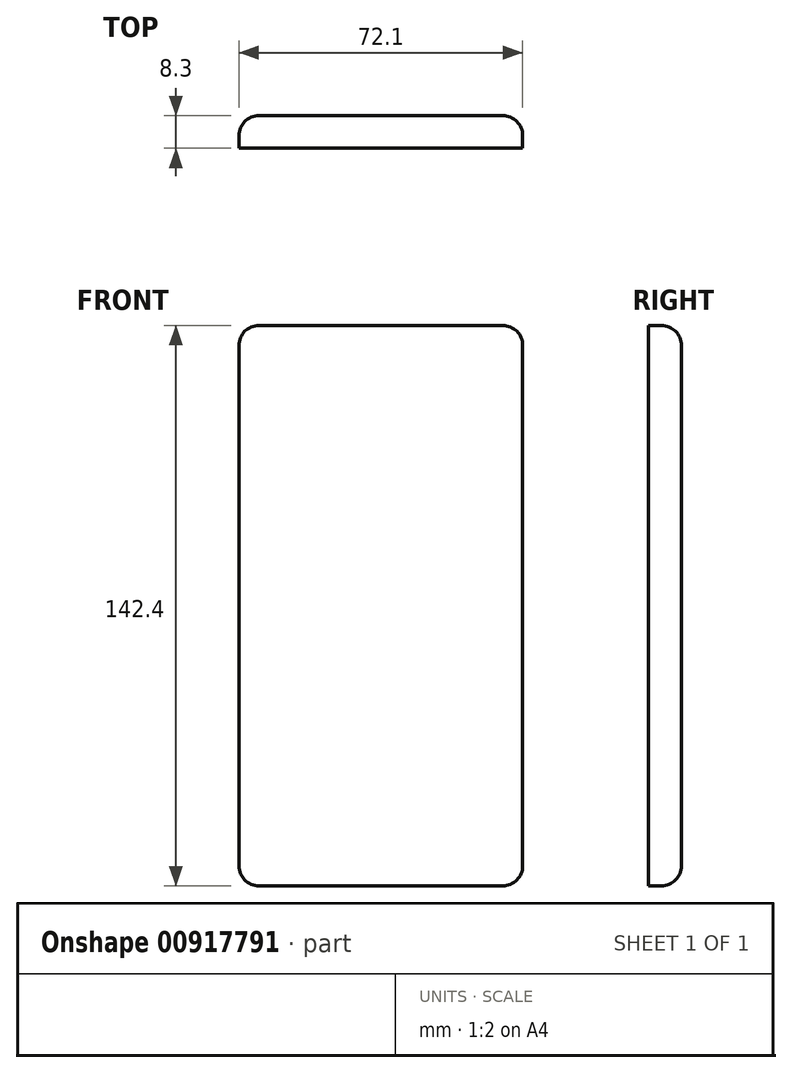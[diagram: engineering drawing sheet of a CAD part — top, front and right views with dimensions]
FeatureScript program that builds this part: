
annotation { "Feature Type Name" : "Feature", "Feature Type Description" : "" }
export const myFeature = defineFeature(function(context is Context, id is Id, definition is map)
    precondition{}
    {
        {
            var Q0;
            Q0=qCreatedBy(makeId("Front.planeOp"),FACE);
            var sketch = newSketch(context, id + "F0", { "sketchPlane" : qUnion([Q0])});
            skLineSegment(sketch, "E0.bottom", {"start": v(36.05, 71.2) * mm, "end": v(-36.05, 71.2) * mm});
            skLineSegment(sketch, "E0.top", {"start": v(36.05, -71.2) * mm, "end": v(-36.05, -71.2) * mm});
            skLineSegment(sketch, "E0.left", {"start": v(36.05, 71.2) * mm, "end": v(36.05, -71.2) * mm});
            skLineSegment(sketch, "E0.right", {"start": v(-36.05, 71.2) * mm, "end": v(-36.05, -71.2) * mm});
            skPoint(sketch, "E0.middle", {"position": v(0, 0) * mm});
            skSolve(sketch);
        }
        {
            var Q0;
            Q0 = qSketchRegion(id + "F0", true);
            extrude(context, id + "F1", {"entities" : qUnion([Q0]), "depth" : 8.3 * mm, "offsetDistance" : 25.4 * mm});
        }
        {
            var Q0;
            Q0=makeQuery(id+"F1.opExtrude","SWEPT_EDGE",EDGE,{"disambiguationData":[OSD([sQuery(id+"F0.wireOp",EDGE,"E0.bottom"),sQuery(id+"F0.wireOp",EDGE,"E0.right")])]});
            var Q1;
            Q1=makeQuery(id+"F1.opExtrude","SWEPT_EDGE",EDGE,{"disambiguationData":[OSD([sQuery(id+"F0.wireOp",EDGE,"E0.bottom"),sQuery(id+"F0.wireOp",EDGE,"E0.left")])]});
            var Q2;
            Q2=makeQuery(id+"F1.opExtrude","SWEPT_EDGE",EDGE,{"disambiguationData":[OSD([sQuery(id+"F0.wireOp",EDGE,"E0.top"),sQuery(id+"F0.wireOp",EDGE,"E0.left")])]});
            var Q3;
            Q3=makeQuery(id+"F1.opExtrude","SWEPT_EDGE",EDGE,{"disambiguationData":[OSD([sQuery(id+"F0.wireOp",EDGE,"E0.top"),sQuery(id+"F0.wireOp",EDGE,"E0.right")])]});
            fillet(context, id + "F2", {"entities" : qUnion([Q0, Q1, Q2, Q3]), "radius" : 5.08 * mm, "tangentPropagation" : true, "allowEdgeOverflow" : false});
        }
        {
            var Q0;
            Q0=makeQuery(id+"F1.opExtrude","CAP_EDGE",EDGE,{"disambiguationData":[OSD([sQuery(id+"F0.wireOp",EDGE,"E0.left")])],"isStart":true});
            fillet(context, id + "F3", {"entities" : qUnion([Q0]), "radius" : 5.08 * mm, "tangentPropagation" : true, "allowEdgeOverflow" : false});
        }
    });
